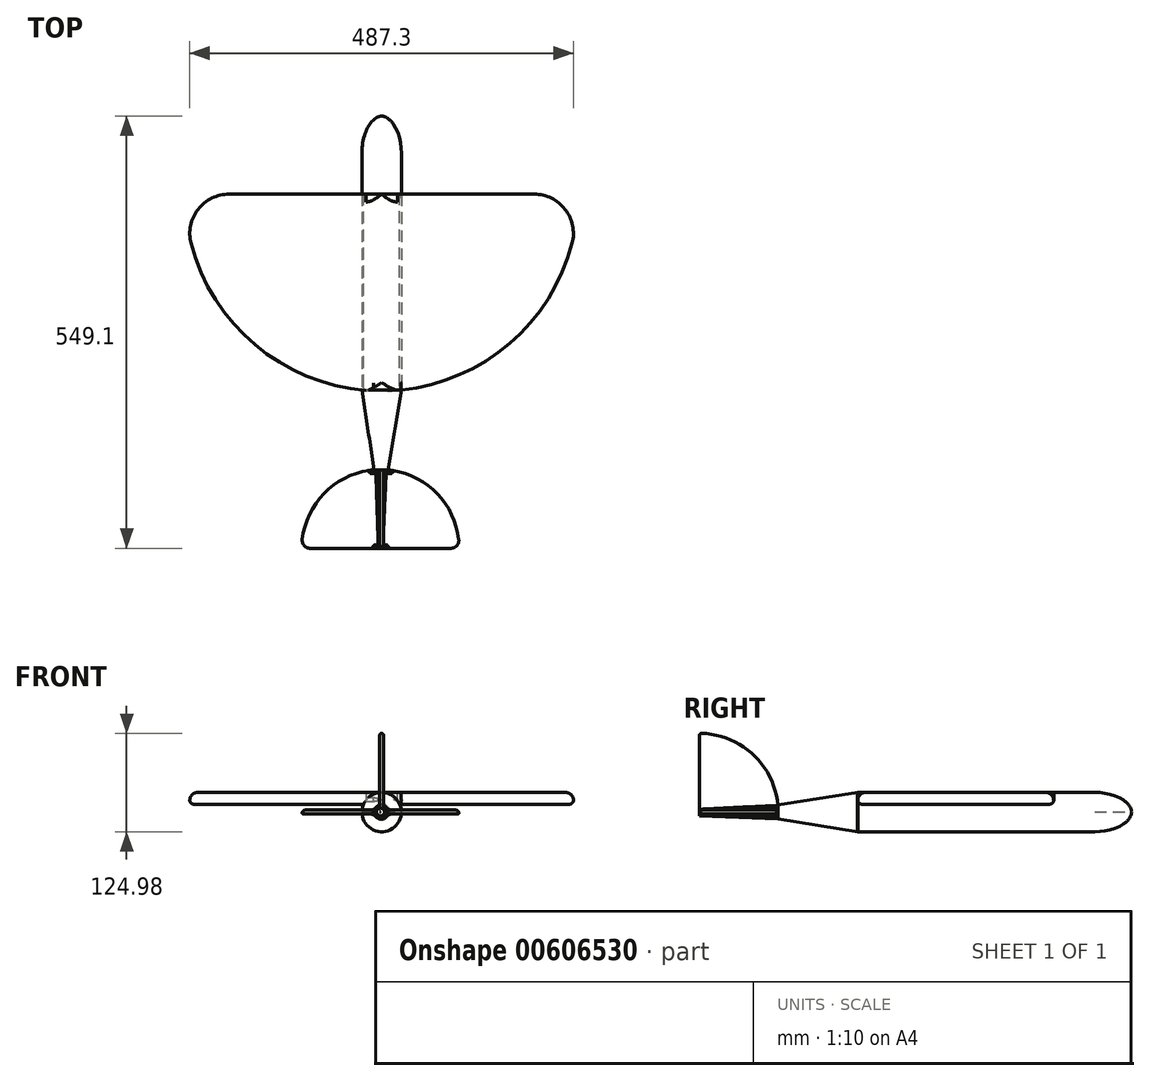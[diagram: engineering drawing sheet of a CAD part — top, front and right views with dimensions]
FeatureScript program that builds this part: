
annotation { "Feature Type Name" : "Feature", "Feature Type Description" : "" }
export const myFeature = defineFeature(function(context is Context, id is Id, definition is map)
    precondition{}
    {
        {
            var Q0;
            Q0=qCreatedBy(makeId("Top.planeOp"),FACE);
            var sketch = newSketch(context, id + "F0", { "sketchPlane" : qUnion([Q0])});
            skArc(sketch, "E0", {"start": v(-242.06, -62.5) * mm, "mid": v(-157.02, -194.54) * mm, "end": v(-10, -249.8) * mm});
            skLineSegment(sketch, "E1", {"start": v(-25, 0) * mm, "end": v(-193.65, 0) * mm});
            skLineSegment(sketch, "E2", {"start": v(10, 0) * mm, "end": v(193.65, 0) * mm});
            skPoint(sketch, "E3.visualSharp", {"position": v(-250, 0) * mm});
            skArc(sketch, "E3.filletArc", {"start": v(-193.65, 0) * mm, "mid": v(-233.18, -19.38) * mm, "end": v(-242.06, -62.5) * mm});
            skPoint(sketch, "E4.visualSharp", {"position": v(250, 0) * mm});
            skArc(sketch, "E4.filletArc", {"start": v(242.06, -62.5) * mm, "mid": v(233.18, -19.38) * mm, "end": v(193.65, 0) * mm});
            skLineSegment(sketch, "E5", {"start": v(0, 0) * mm, "end": v(0, -249.5) * mm});
            skArc(sketch, "E6", {"start": v(98.63, -450) * mm, "mid": v(-1.37, -350) * mm, "end": v(-101.37, -450) * mm});
            skLineSegment(sketch, "E7", {"start": v(-1.37, -450) * mm, "end": v(-101.37, -450) * mm});
            skLineSegment(sketch, "E8", {"start": v(-1.37, -450) * mm, "end": v(98.63, -450) * mm});
            skLineSegment(sketch, "E9", {"start": v(6.8, -350.32) * mm, "end": v(3.63, -450) * mm});
            skLineSegment(sketch, "E10.MirrorCS", {"start": v(-9.54, -350.32) * mm, "end": v(-6.37, -450) * mm});
            skPoint(sketch, "E11.MirrorCS.start.orphan", {"position": v(-10, 0) * mm});
            skLineSegment(sketch, "E12", {"start": v(25, 0) * mm, "end": v(25, -248.75) * mm});
            skLineSegment(sketch, "E13", {"start": v(6.8, -350.32) * mm, "end": v(25, -248.75) * mm});
            skLineSegment(sketch, "E14", {"start": v(-1.37, -450) * mm, "end": v(0, -249.5) * mm});
            skArc(sketch, "E15.trimOffspring", {"start": v(25, -248.75) * mm, "mid": v(162.8, -189.73) * mm, "end": v(242.06, -62.5) * mm});
            skLineSegment(sketch, "E16", {"start": v(-25, 0) * mm, "end": v(-10, 0) * mm});
            skLineSegment(sketch, "E17", {"start": v(25, -248.75) * mm, "end": v(-10, -249.8) * mm});
            skLineSegment(sketch, "E18", {"start": v(10, 0) * mm, "end": v(-10, 0) * mm});
            skLineSegment(sketch, "E19", {"start": v(0, 0) * mm, "end": v(0, 99.04) * mm});
            skLineSegment(sketch, "E20", {"start": v(25, 0) * mm, "end": v(25, 52.2) * mm});
            skLineSegment(sketch, "E21", {"start": v(-25, 0) * mm, "end": v(-25, -248.75) * mm});
            skLineSegment(sketch, "E22", {"start": v(-25, 0) * mm, "end": v(-25, 52.2) * mm});
            skFitSpline(sketch, "E23", {"points": [v(-25, 52.2) * mm, v(0, 99.04) * mm, v(25, 52.2) * mm], "startDerivative": vector(0, 156.33) * mm, "endDerivative": vector(0, -161.8) * mm});
            skLineSegment(sketch, "E24", {"start": v(-9.54, -350.32) * mm, "end": v(-25, -248.75) * mm});
            skSolve(sketch);
        }
        {
            var Q0;
            {var subQ0=sQuery(id+"F0.wireOp",EDGE,"E7");var subQ1=sQuery(id+"F0.wireOp",EDGE,"E6");var subQ2=makeQuery(id+"F0.imprint","INTERSECT",VERTEX,{"derivedFrom":[subQ1,subQ0]});Q0=makeQuery(id+"F0.imprint","IMPRINT",FACE,{"disambiguationData":[TD([[makeQuery(id+"F0.imprint","IMPRINT",EDGE,{"disambiguationData":[TD([[subQ2,1.0]])],"derivedFrom":subQ1}),1.0]])]});}
            var Q1;
            {var subQ0=sQuery(id+"F0.wireOp",EDGE,"E8");var subQ1=sQuery(id+"F0.wireOp",EDGE,"E6");var subQ2=makeQuery(id+"F0.imprint","INTERSECT",VERTEX,{"derivedFrom":[subQ1,subQ0]});Q1=makeQuery(id+"F0.imprint","IMPRINT",FACE,{"disambiguationData":[TD([[makeQuery(id+"F0.imprint","IMPRINT",EDGE,{"disambiguationData":[TD([[subQ2,-1.0]])],"derivedFrom":subQ1}),1.0]])]});}
            var Q2;
            {var subQ3=sQuery(id+"F0.wireOp",EDGE,"E6");var subQ5=sQuery(id+"F0.wireOp",EDGE,"E9");var subQ6=makeQuery(id+"F0.imprint","INTERSECT",VERTEX,{"derivedFrom":[subQ3,subQ5]});Q2=makeQuery(id+"F0.imprint","IMPRINT",FACE,{"disambiguationData":[TD([[makeQuery(id+"F0.imprint","IMPRINT",EDGE,{"disambiguationData":[TD([[subQ6,-1.0]])],"derivedFrom":subQ3}),1.0]])]});}
            var Q3;
            {var subQ3=sQuery(id+"F0.wireOp",EDGE,"E6");var subQ5=sQuery(id+"F0.wireOp",EDGE,"E10.MirrorCS");var subQ7=makeQuery(id+"F0.imprint","INTERSECT",VERTEX,{"derivedFrom":[subQ3,subQ5]});Q3=makeQuery(id+"F0.imprint","IMPRINT",FACE,{"disambiguationData":[TD([[makeQuery(id+"F0.imprint","IMPRINT",EDGE,{"disambiguationData":[TD([[subQ7,1.0]])],"derivedFrom":subQ3}),1.0]])]});}
            extrude(context, id + "F1", {"entities" : qUnion([Q0, Q1, Q2, Q3]), "endBound" : BoundingType.SYMMETRIC, "depth" : 5 * mm, "offsetDistance" : 25 * mm});
        }
        {
            var Q0;
            Q0=makeQuery(id+"F1.opExtrude","SWEPT_EDGE",EDGE,{"disambiguationData":[OSD([sQuery(id+"F0.wireOp",EDGE,"E6"),sQuery(id+"F0.wireOp",EDGE,"E7")])]});
            var Q1;
            Q1=makeQuery(id+"F1.opExtrude","SWEPT_EDGE",EDGE,{"disambiguationData":[OSD([sQuery(id+"F0.wireOp",EDGE,"E6"),sQuery(id+"F0.wireOp",EDGE,"E8")])]});
            fillet(context, id + "F2", {"entities" : qUnion([Q0, Q1]), "radius" : 10 * mm, "tangentPropagation" : true, "allowEdgeOverflow" : false});
        }
        {
            var Q0;
            Q0=makeQuery(id+"F1.boolean.opBoolean","SPLIT",EDGE,{"disambiguationData":[OD(0.0)],"derivedFrom":makeQuery(id+"F1.opExtrude","CAP_EDGE",EDGE,{"disambiguationData":[OSD([sQuery(id+"F0.wireOp",EDGE,"E6")])],"isStart":false})});
            var Q1;
            Q1=makeQuery(id+"F1.boolean.opBoolean","SPLIT",EDGE,{"disambiguationData":[OD(1.0)],"derivedFrom":makeQuery(id+"F1.opExtrude","CAP_EDGE",EDGE,{"disambiguationData":[OSD([sQuery(id+"F0.wireOp",EDGE,"E6")])],"isStart":false})});
            fillet(context, id + "F3", {"entities" : qUnion([Q0, Q1]), "radius" : 4 * mm, "tangentPropagation" : true, "allowEdgeOverflow" : false});
        }
        {
            var Q0;
            Q0=makeQuery(id+"F1.boolean.opBoolean","SPLIT",EDGE,{"disambiguationData":[OD(0.0)],"derivedFrom":makeQuery(id+"F1.opExtrude","CAP_EDGE",EDGE,{"disambiguationData":[OSD([sQuery(id+"F0.wireOp",EDGE,"E6")])],"isStart":true})});
            var Q1;
            Q1=makeQuery(id+"F1.boolean.opBoolean","SPLIT",EDGE,{"disambiguationData":[OD(1.0)],"derivedFrom":makeQuery(id+"F1.opExtrude","CAP_EDGE",EDGE,{"disambiguationData":[OSD([sQuery(id+"F0.wireOp",EDGE,"E6")])],"isStart":true})});
            fillet(context, id + "F4", {"entities" : qUnion([Q0, Q1]), "radius" : 1 * mm, "tangentPropagation" : true, "allowEdgeOverflow" : false});
        }
        {
            var Q0;
            {var subQ0=sQuery(id+"F0.wireOp",EDGE,"E3.filletArc");Q0=makeQuery(id+"F0.imprint","IMPRINT",FACE,{"disambiguationData":[TD([[makeQuery(id+"F0.imprint","IMPRINT",EDGE,{"derivedFrom":subQ0}),1.0]])]});}
            cPlane(context, id + "F5", {"entities" : qUnion([Q0]), "cplaneType" : CPlaneType.OFFSET, "offset" : 18 * mm, "oppositeDirection" : true, "width" : 150 * mm, "height" : 150 * mm});
        }
        {
            var Q0;
            {var subQ0=sQuery(id+"F0.wireOp",EDGE,"E3.filletArc");Q0=makeQuery(id+"F0.imprint","IMPRINT",FACE,{"disambiguationData":[TD([[makeQuery(id+"F0.imprint","IMPRINT",EDGE,{"derivedFrom":subQ0}),1.0]])]});}
            cPlane(context, id + "F6", {"entities" : qUnion([Q0]), "cplaneType" : CPlaneType.OFFSET, "offset" : 25 * mm, "width" : 150 * mm, "height" : 150 * mm});
        }
        {
            var Q0;
            Q0=qCreatedBy(id+"F6.planeOp",FACE);
            var sketch = newSketch(context, id + "F7", { "sketchPlane" : qUnion([Q0])});
            skLineSegment(sketch, "E25.0", {"start": v(-25, 0) * mm, "end": v(-193.65, 0) * mm});
            skLineSegment(sketch, "E26.0", {"start": v(10, 0) * mm, "end": v(193.65, 0) * mm});
            skArc(sketch, "E27.0", {"start": v(-242.06, -62.5) * mm, "mid": v(-157.02, -194.54) * mm, "end": v(-10, -249.8) * mm});
            skArc(sketch, "E28.0", {"start": v(-193.65, 0) * mm, "mid": v(-233.18, -19.38) * mm, "end": v(-242.06, -62.5) * mm});
            skArc(sketch, "E29.0", {"start": v(242.06, -62.5) * mm, "mid": v(233.18, -19.38) * mm, "end": v(193.65, 0) * mm});
            skArc(sketch, "E30.0", {"start": v(25, -248.75) * mm, "mid": v(162.8, -189.73) * mm, "end": v(242.06, -62.5) * mm});
            skLineSegment(sketch, "E31.0", {"start": v(-25, 0) * mm, "end": v(-10, 0) * mm});
            skLineSegment(sketch, "E32", {"start": v(10, 0) * mm, "end": v(-10, 0) * mm});
            skLineSegment(sketch, "E33", {"start": v(25, -248.75) * mm, "end": v(-10, -249.8) * mm});
            skSolve(sketch);
        }
        {
            var Q0;
            Q0=makeQuery(id+"F7.imprint","IMPRINT",FACE,{"disambiguationData":[TD([[makeQuery(id+"F7.imprint","IMPRINT",EDGE,{"derivedFrom":sQuery(id+"F7.wireOp",EDGE,"E25.0")}),1.0]])]});
            extrude(context, id + "F8", {"entities" : qUnion([Q0]), "oppositeDirection" : true, "depth" : 15 * mm, "offsetDistance" : 25 * mm});
        }
        {
            var Q0;
            Q0=qCreatedBy(makeId("Right.planeOp"),FACE);
            var sketch = newSketch(context, id + "F9", { "sketchPlane" : qUnion([Q0])});
            skPoint(sketch, "E34.0", {"position": v(-350, 0) * mm});
            skPoint(sketch, "E35.0", {"position": v(-450, 0) * mm});
            skLineSegment(sketch, "E36.0", {"start": v(-450, 0) * mm, "end": v(-249.5, 0) * mm});
            skArc(sketch, "E37", {"start": v(-350, 0) * mm, "mid": v(-379.28, 70.71) * mm, "end": v(-450, 100) * mm});
            skLineSegment(sketch, "E38", {"start": v(-450, 0) * mm, "end": v(-450, 100) * mm});
            skSolve(sketch);
        }
        {
            var Q0;
            {var subQ2=sQuery(id+"F9.wireOp",EDGE,"E37");Q0=makeQuery(id+"F9.imprint","IMPRINT",FACE,{"disambiguationData":[TD([[makeQuery(id+"F9.imprint","IMPRINT",EDGE,{"derivedFrom":subQ2}),1.0]])]});}
            extrude(context, id + "F10", {"entities" : qUnion([Q0]), "endBound" : BoundingType.SYMMETRIC, "depth" : 5 * mm, "offsetDistance" : 25 * mm});
        }
        {
            var Q0;
            Q0=makeQuery(id+"F8.opExtrude","CAP_FACE",FACE,{"disambiguationData":[OSD([sQuery(id+"F7.wireOp",EDGE,"E25.0"),sQuery(id+"F7.wireOp",EDGE,"E26.0"),sQuery(id+"F7.wireOp",EDGE,"E27.0"),sQuery(id+"F7.wireOp",EDGE,"E28.0"),sQuery(id+"F7.wireOp",EDGE,"E29.0")])],"isStart":false});
            fillet(context, id + "F11", {"entities" : qUnion([Q0]), "radius" : 5 * mm, "tangentPropagation" : true, "allowEdgeOverflow" : false});
        }
        {
            var Q0;
            Q0=makeQuery(id+"F10.opExtrude","CAP_EDGE",EDGE,{"disambiguationData":[OSD([sQuery(id+"F9.wireOp",EDGE,"E37")])],"isStart":true});
            var Q1;
            Q1=makeQuery(id+"F10.opExtrude","CAP_EDGE",EDGE,{"disambiguationData":[OSD([sQuery(id+"F9.wireOp",EDGE,"E37")])],"isStart":false});
            var Q2;
            Q2=makeQuery(id+"F10.opExtrude","SWEPT_EDGE",EDGE,{"disambiguationData":[OSD([sQuery(id+"F9.wireOp",EDGE,"E37"),sQuery(id+"F9.wireOp",EDGE,"E38")])]});
            fillet(context, id + "F12", {"entities" : qUnion([Q0, Q1, Q2]), "radius" : 2.5 * mm, "tangentPropagation" : true, "allowEdgeOverflow" : false});
        }
        {
            var Q0;
            {var subQ0=sQuery(id+"F0.wireOp",EDGE,"d04ff355-46b1-4c78-82ed-6dda78510cc6");var subQ1=sQuery(id+"F0.wireOp",EDGE,"E19");var subQ2=makeQuery(id+"F0.imprint","INTERSECT",VERTEX,{"derivedFrom":[subQ1,subQ0]});Q0=makeQuery(id+"F0.imprint","IMPRINT",FACE,{"disambiguationData":[TD([[makeQuery(id+"F0.imprint","IMPRINT",EDGE,{"disambiguationData":[TD([[subQ2,1.0]])],"derivedFrom":subQ1}),1.0]])]});}
            var Q1;
            Q1=sQuery(id+"F0.wireOp",EDGE,"E19");
            revolve(context, id + "F13", {"operationType" : NewBodyOperationType.ADD, "entities" : qUnion([Q0]), "axis" : qUnion([Q1]), "revolveType" : RevolveType.FULL});
        }
        {
            var Q0;
            {var subQ0=sQuery(id+"F0.wireOp",EDGE,"E10.MirrorCS");Q0=makeQuery(id+"F0.imprint","IMPRINT",FACE,{"disambiguationData":[TD([[makeQuery(id+"F0.imprint","IMPRINT",EDGE,{"derivedFrom":subQ0}),1.0]])]});}
            var Q1;
            Q1=sQuery(id+"F0.wireOp",EDGE,"E14");
            revolve(context, id + "F14", {"operationType" : NewBodyOperationType.ADD, "entities" : qUnion([Q0]), "axis" : qUnion([Q1]), "revolveType" : RevolveType.FULL});
        }
        {
            var Q0;
            Q0=makeQuery(id+"F8.opExtrude","CAP_FACE",FACE,{"disambiguationData":[OSD([sQuery(id+"F7.wireOp",EDGE,"E25.0"),sQuery(id+"F7.wireOp",EDGE,"E26.0"),sQuery(id+"F7.wireOp",EDGE,"E27.0"),sQuery(id+"F7.wireOp",EDGE,"E28.0"),sQuery(id+"F7.wireOp",EDGE,"E29.0"),sQuery(id+"F7.wireOp",EDGE,"E30.0"),sQuery(id+"F7.wireOp",EDGE,"E31.0"),sQuery(id+"F7.wireOp",EDGE,"E32"),sQuery(id+"F7.wireOp",EDGE,"E33")])],"isStart":true});
            fillet(context, id + "F15", {"entities" : qUnion([Q0]), "radius" : 10 * mm, "tangentPropagation" : true, "allowEdgeOverflow" : false});
        }
        {
            var Q0;
            Q0=makeQuery(id+"F14.boolean.opBoolean","INTERSECT",EDGE,{"disambiguationData":[OD(0.0)],"derivedFrom":[makeQuery(id+"F1.opExtrude","CAP_FACE",FACE,{"disambiguationData":[OSD([sQuery(id+"F0.wireOp",EDGE,"E6"),sQuery(id+"F0.wireOp",EDGE,"E7"),sQuery(id+"F0.wireOp",EDGE,"E8")])],"isStart":false}),makeQuery(id+"F14.opRevolve","SWEPT_FACE",FACE,{"disambiguationData":[OSD([sQuery(id+"F0.wireOp",EDGE,"E10.MirrorCS")])]})]});
            var Q1;
            Q1=makeQuery(id+"F14.boolean.opBoolean","INTERSECT",EDGE,{"disambiguationData":[OD(1.0)],"derivedFrom":[makeQuery(id+"F1.opExtrude","CAP_FACE",FACE,{"disambiguationData":[OSD([sQuery(id+"F0.wireOp",EDGE,"E6"),sQuery(id+"F0.wireOp",EDGE,"E7"),sQuery(id+"F0.wireOp",EDGE,"E8")])],"isStart":false}),makeQuery(id+"F14.opRevolve","SWEPT_FACE",FACE,{"disambiguationData":[OSD([sQuery(id+"F0.wireOp",EDGE,"E10.MirrorCS")])]})]});
            fillet(context, id + "F16", {"entities" : qUnion([Q0, Q1]), "radius" : 10 * mm, "tangentPropagation" : true, "allowEdgeOverflow" : false});
        }
        {
            var Q0;
            {var subQ0=sQuery(id+"F0.wireOp",EDGE,"E16");Q0=makeQuery(id+"F0.imprint","IMPRINT",FACE,{"disambiguationData":[TD([[makeQuery(id+"F0.imprint","IMPRINT",EDGE,{"derivedFrom":subQ0}),-1.0]])]});}
            var Q1;
            Q1=sQuery(id+"F0.wireOp",EDGE,"E5");
            revolve(context, id + "F17", {"operationType" : NewBodyOperationType.ADD, "entities" : qUnion([Q0]), "axis" : qUnion([Q1]), "revolveType" : RevolveType.FULL});
        }
        {
            var Q0;
            {var subQ5=sQuery(id+"F0.wireOp",EDGE,"E24");Q0=makeQuery(id+"F0.imprint","IMPRINT",FACE,{"disambiguationData":[TD([[makeQuery(id+"F0.imprint","IMPRINT",EDGE,{"derivedFrom":subQ5}),-1.0]])]});}
            var Q1;
            Q1=sQuery(id+"F0.wireOp",EDGE,"E14");
            revolve(context, id + "F18", {"operationType" : NewBodyOperationType.ADD, "entities" : qUnion([Q0]), "axis" : qUnion([Q1]), "revolveType" : RevolveType.FULL});
        }
    });
